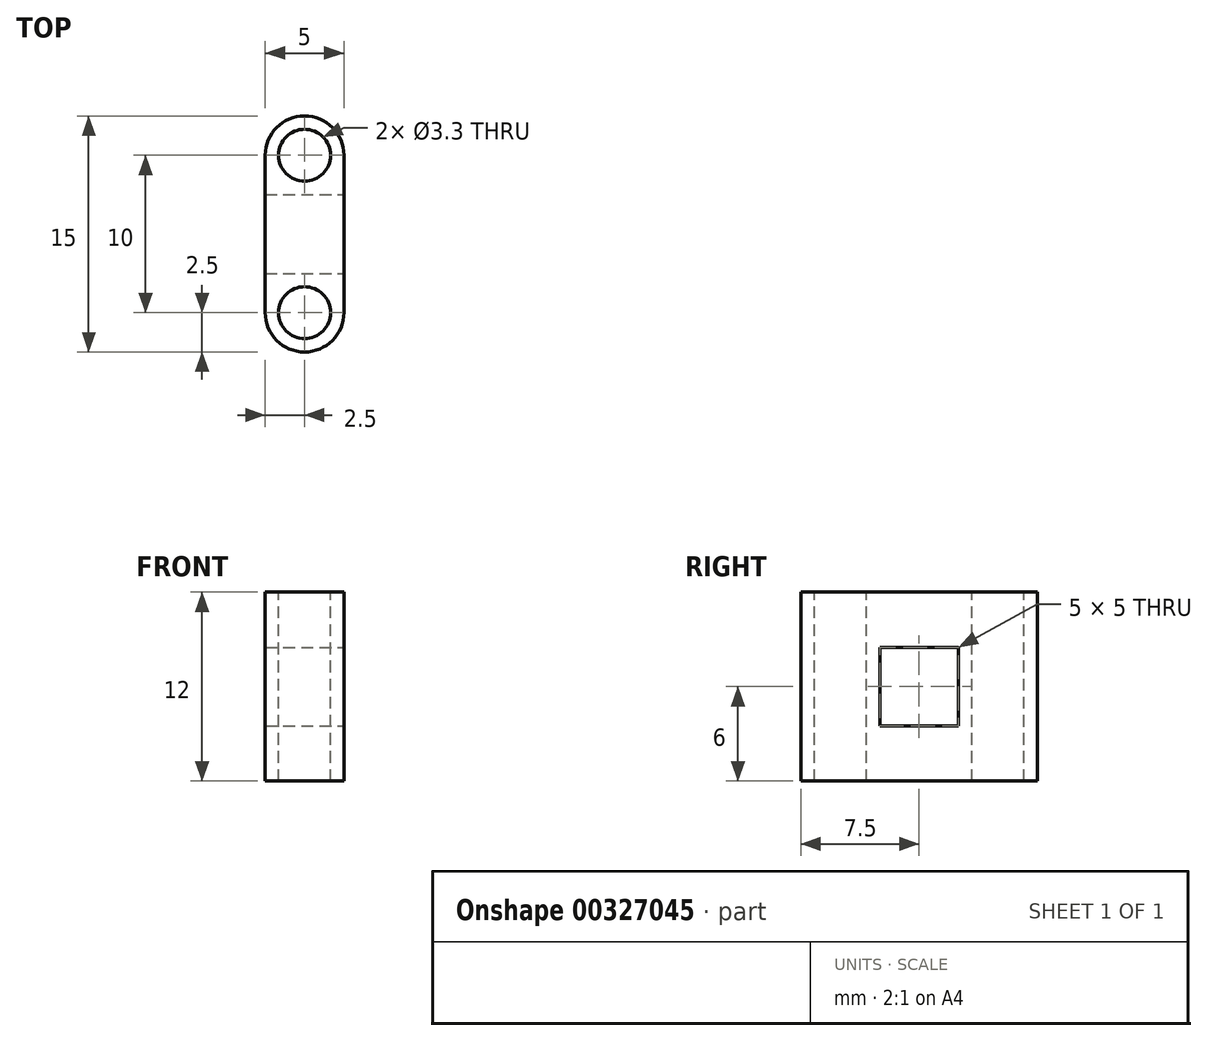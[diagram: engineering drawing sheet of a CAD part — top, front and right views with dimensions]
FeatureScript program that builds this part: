
annotation { "Feature Type Name" : "Feature", "Feature Type Description" : "" }
export const myFeature = defineFeature(function(context is Context, id is Id, definition is map)
    precondition{}
    {
        {
            var Q0;
            Q0=qCreatedBy(makeId("Top.planeOp"),FACE);
            var sketch = newSketch(context, id + "F0", { "sketchPlane" : qUnion([Q0])});
            skLineSegment(sketch, "E0", {"start": v(0, 0) * mm, "end": v(0, 5) * mm, "construction": true});
            skLineSegment(sketch, "E1", {"start": v(0, 0) * mm, "end": v(0, -5) * mm, "construction": true});
            skLineSegment(sketch, "E2.bottom", {"start": v(-2.5, 7.5) * mm, "end": v(2.5, 7.5) * mm});
            skLineSegment(sketch, "E2.top", {"start": v(-2.5, -7.5) * mm, "end": v(2.5, -7.5) * mm});
            skLineSegment(sketch, "E2.left", {"start": v(-2.5, 7.5) * mm, "end": v(-2.5, -7.5) * mm});
            skLineSegment(sketch, "E2.right", {"start": v(2.5, 7.5) * mm, "end": v(2.5, -7.5) * mm});
            skLineSegment(sketch, "E3", {"start": v(2.5, 0) * mm, "end": v(0, 0) * mm, "construction": true});
            skLineSegment(sketch, "E4", {"start": v(0, 5) * mm, "end": v(0, 7.5) * mm, "construction": true});
            skSolve(sketch);
        }
        {
            var Q0;
            Q0=makeQuery(id+"F0.imprint","IMPRINT",FACE,{"disambiguationData":[TD([[makeQuery(id+"F0.imprint","IMPRINT",EDGE,{"derivedFrom":sQuery(id+"F0.wireOp",EDGE,"E2.bottom")}),-1.0]])]});
            extrude(context, id + "F1", {"entities" : qUnion([Q0]), "depth" : 12 * mm});
        }
        {
            var Q0;
            Q0=makeQuery(id+"F1.opExtrude","SWEPT_FACE",FACE,{"disambiguationData":[OSD([sQuery(id+"F0.wireOp",EDGE,"E2.right")])]});
            var sketch = newSketch(context, id + "F2", { "sketchPlane" : qUnion([Q0])});
            skLineSegment(sketch, "E5.bottom", {"start": v(2.5, 8.5) * mm, "end": v(-2.5, 8.5) * mm});
            skLineSegment(sketch, "E5.top", {"start": v(2.5, 3.5) * mm, "end": v(-2.5, 3.5) * mm});
            skLineSegment(sketch, "E5.left", {"start": v(2.5, 8.5) * mm, "end": v(2.5, 3.5) * mm});
            skLineSegment(sketch, "E5.right", {"start": v(-2.5, 8.5) * mm, "end": v(-2.5, 3.5) * mm});
            skPoint(sketch, "E5.middle", {"position": v(0, 6) * mm});
            skPoint(sketch, "E5.middle.positionSnap0", {"position": v(-7.5, 6) * mm});
            skPoint(sketch, "E5.middle.positionSnap1", {"position": v(0, 12) * mm});
            skPoint(sketch, "E5.centerSnap0", {"position": v(-7.5, 6) * mm});
            skPoint(sketch, "E5.centerSnap1", {"position": v(0, 12) * mm});
            skSolve(sketch);
        }
        {
            var Q0;
            Q0=makeQuery(id+"F2.imprint","IMPRINT",FACE,{"disambiguationData":[TD([[makeQuery(id+"F2.imprint","IMPRINT",EDGE,{"derivedFrom":sQuery(id+"F2.wireOp",EDGE,"E5.bottom")}),1.0]])]});
            extrude(context, id + "F3", {"entities" : qUnion([Q0]), "operationType" : NewBodyOperationType.REMOVE, "endBound" : BoundingType.UP_TO_NEXT, "oppositeDirection" : true, "depth" : 25 * mm});
        }
        {
            var Q0;
            Q0=makeQuery(id+"F1.opExtrude","SWEPT_EDGE",EDGE,{"disambiguationData":[OSD([sQuery(id+"F0.wireOp",EDGE,"E2.top"),sQuery(id+"F0.wireOp",EDGE,"E2.right")])]});
            var Q1;
            Q1=makeQuery(id+"F1.opExtrude","SWEPT_EDGE",EDGE,{"disambiguationData":[OSD([sQuery(id+"F0.wireOp",EDGE,"E2.top"),sQuery(id+"F0.wireOp",EDGE,"E2.left")])]});
            var Q2;
            Q2=makeQuery(id+"F1.opExtrude","SWEPT_EDGE",EDGE,{"disambiguationData":[OSD([sQuery(id+"F0.wireOp",EDGE,"E2.bottom"),sQuery(id+"F0.wireOp",EDGE,"E2.right")])]});
            var Q3;
            Q3=makeQuery(id+"F1.opExtrude","SWEPT_EDGE",EDGE,{"disambiguationData":[OSD([sQuery(id+"F0.wireOp",EDGE,"E2.bottom"),sQuery(id+"F0.wireOp",EDGE,"E2.left")])]});
            var Q4;
            Q4=makeQuery(id+"F3.boolean.opBoolean","COPY",EDGE,{"derivedFrom":makeQuery(id+"F3.opExtrude","TWEAK_EDGE",EDGE,{"derivedFrom":[makeQuery(id+"F1.opExtrude","SWEPT_FACE",FACE,{"disambiguationData":[OSD([sQuery(id+"F0.wireOp",EDGE,"E2.left")])]}),makeQuery(id+"F2.imprint","IMPRINT",EDGE,{"derivedFrom":sQuery(id+"F2.wireOp",EDGE,"E5.left")})]})});
            var Q5;
            Q5=makeQuery(id+"F3.boolean.opBoolean","COPY",EDGE,{"derivedFrom":makeQuery(id+"F3.opExtrude","TWEAK_EDGE",EDGE,{"derivedFrom":[makeQuery(id+"F1.opExtrude","SWEPT_FACE",FACE,{"disambiguationData":[OSD([sQuery(id+"F0.wireOp",EDGE,"E2.left")])]}),makeQuery(id+"F2.imprint","IMPRINT",EDGE,{"derivedFrom":sQuery(id+"F2.wireOp",EDGE,"E5.right")})]})});
            var Q6;
            Q6=makeQuery(id+"F3.boolean.opBoolean","COPY",EDGE,{"derivedFrom":makeQuery(id+"F3.opExtrude","CAP_EDGE",EDGE,{"disambiguationData":[OSD([sQuery(id+"F2.wireOp",EDGE,"E5.right")])],"isStart":true})});
            var Q7;
            Q7=makeQuery(id+"F3.boolean.opBoolean","COPY",EDGE,{"derivedFrom":makeQuery(id+"F3.opExtrude","CAP_EDGE",EDGE,{"disambiguationData":[OSD([sQuery(id+"F2.wireOp",EDGE,"E5.left")])],"isStart":true})});
            fillet(context, id + "F4", {"entities" : qUnion([Q0, Q1, Q2, Q3, Q4, Q5, Q6, Q7]), "radius" : 2.5 * mm, "tangentPropagation" : true, "allowEdgeOverflow" : false});
        }
        {
            var Q0;
            Q0=makeQuery(id+"F1.opExtrude","CAP_FACE",FACE,{"disambiguationData":[OSD([sQuery(id+"F0.wireOp",EDGE,"E2.bottom"),sQuery(id+"F0.wireOp",EDGE,"E2.top"),sQuery(id+"F0.wireOp",EDGE,"E2.left"),sQuery(id+"F0.wireOp",EDGE,"E2.right")])],"isStart":false});
            var sketch = newSketch(context, id + "F5", { "sketchPlane" : qUnion([Q0])});
            skLineSegment(sketch, "E6", {"start": v(0, -5) * mm, "end": v(0, 5) * mm, "construction": true});
            skSolve(sketch);
        }
        {
            var Q0;
            Q0=sQuery(id+"F5.wireOp",VERTEX,"E6.end");
            var Q1;
            Q1=sQuery(id+"F5.wireOp",VERTEX,"E6.start");
            var Q2;
            Q2=makeQuery(id+"F1.opExtrude","SWEPT_BODY",BODY,{"disambiguationData":[OSD([sQuery(id+"F0.wireOp",EDGE,"E2.bottom"),sQuery(id+"F0.wireOp",EDGE,"E2.top"),sQuery(id+"F0.wireOp",EDGE,"E2.left"),sQuery(id+"F0.wireOp",EDGE,"E2.right")])]});
            hole(context, id + "F6", {"style" : HoleStyle.SIMPLE, "endStyle" : HoleEndStyle.THROUGH, "standardTappedOrClearance" : lookupTablePath({ "standard" : "ISO", "fit" : "Normal", "size" : "M3", "type" : "Clearance" }), "standardBlindInLast" : lookupTablePath({ "fit" : "Standard", "standard" : "ISO", "size" : "M3", "type" : "Clearance" }), "holeDiameter" : 3.3 * mm, "tappedDepth" : 12 * mm, "tapClearance" : 3, "locations" : qUnion([Q0, Q1]), "scope" : qUnion([Q2])});
        }
    });
